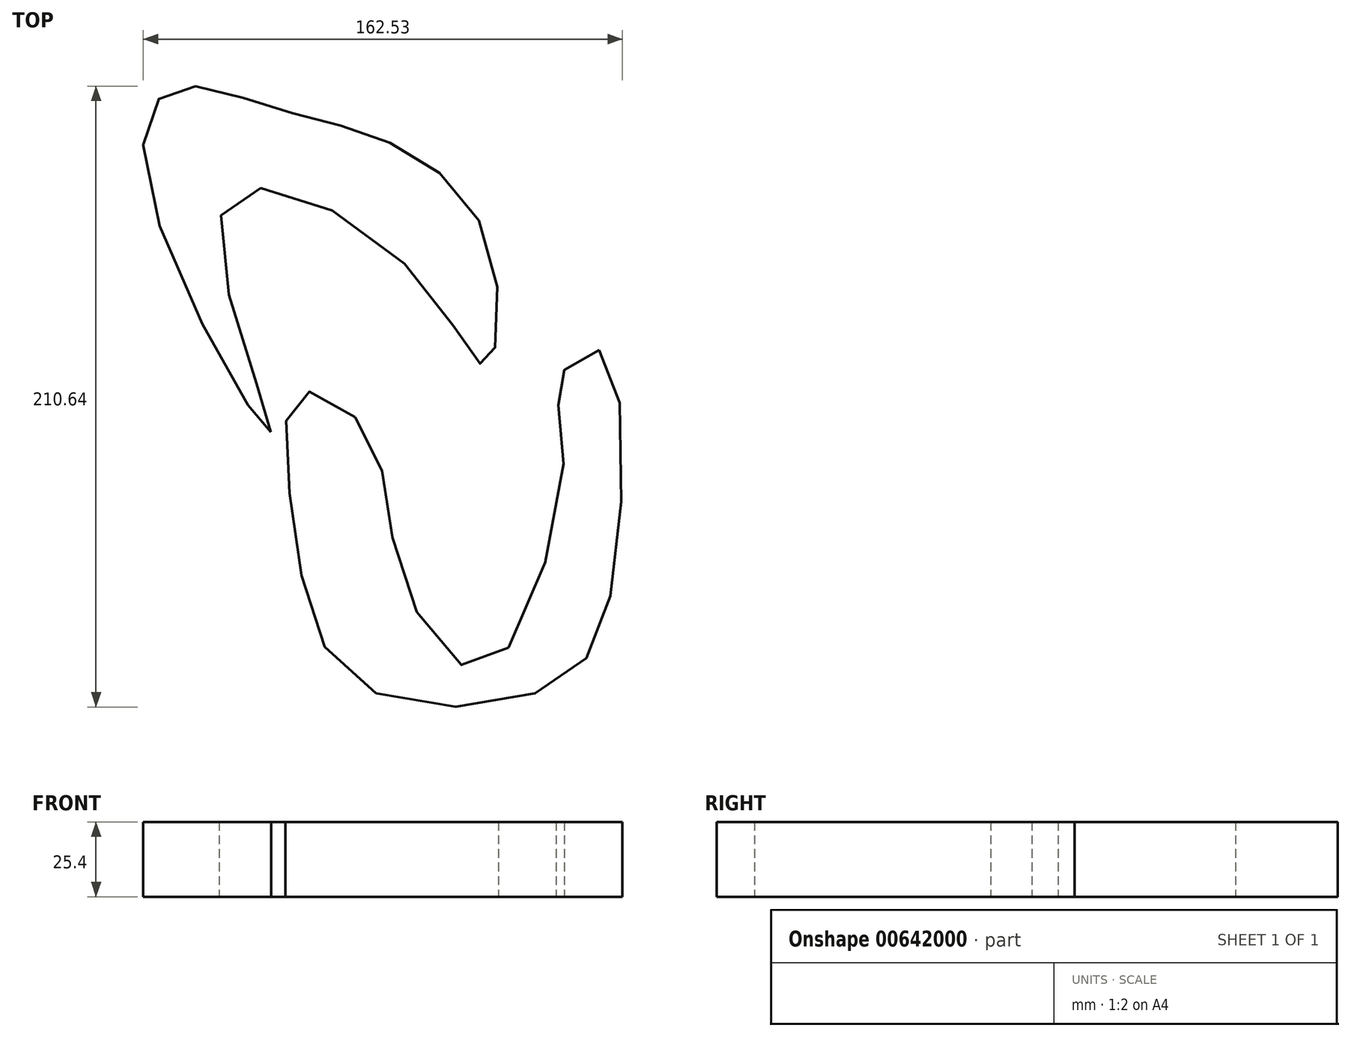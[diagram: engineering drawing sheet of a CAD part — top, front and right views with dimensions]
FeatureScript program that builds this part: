
annotation { "Feature Type Name" : "Feature", "Feature Type Description" : "" }
export const myFeature = defineFeature(function(context is Context, id is Id, definition is map)
    precondition{}
    {
        {
            var Q0;
            Q0=qCreatedBy(makeId("Top.planeOp"),FACE);
            var sketch = newSketch(context, id + "F0", { "sketchPlane" : qUnion([Q0])});
            skFitSpline(sketch, "E0", {"points": [v(38.12, 57.2) * mm, v(43.45, -17.17) * mm, v(21.19, -57.33) * mm, v(-43.77, -55.93) * mm, v(-65.75, 0) * mm, v(-63.74, 42.33) * mm, v(-40.82, 29.63) * mm, v(-29, -18.82) * mm, v(0, -50.4) * mm, v(26.2, 27.36) * mm, v(24.24, 46.72) * mm, v(38.12, 57.2) * mm]});
            skSolve(sketch);
        }
        {
            var Q0;
            Q0 = qSketchRegion(id + "F0", true);
            extrude(context, id + "F1", {"entities" : qUnion([Q0]), "depth" : 25.4 * mm, "offsetDistance" : 25.4 * mm});
        }
        {
            var Q0;
            Q0=qCreatedBy(makeId("Top.planeOp"),FACE);
            var sketch = newSketch(context, id + "F2", { "sketchPlane" : qUnion([Q0])});
            skFitSpline(sketch, "E1", {"points": [v(-73.22, 29.3) * mm, v(-89.25, 105.47) * mm, v(-28.06, 86.7) * mm, v(0, 52.1) * mm, v(0, 95.09) * mm, v(-36.82, 129.16) * mm, v(-72.55, 139.43) * mm, v(-105.24, 146.09) * mm, v(-114.93, 112.88) * mm, v(-73.22, 29.3) * mm]});
            skSolve(sketch);
        }
        {
            var Q0;
            Q0 = qSketchRegion(id + "F2", true);
            extrude(context, id + "F3", {"entities" : qUnion([Q0]), "depth" : 25.4 * mm, "offsetDistance" : 25.4 * mm});
        }
    });
